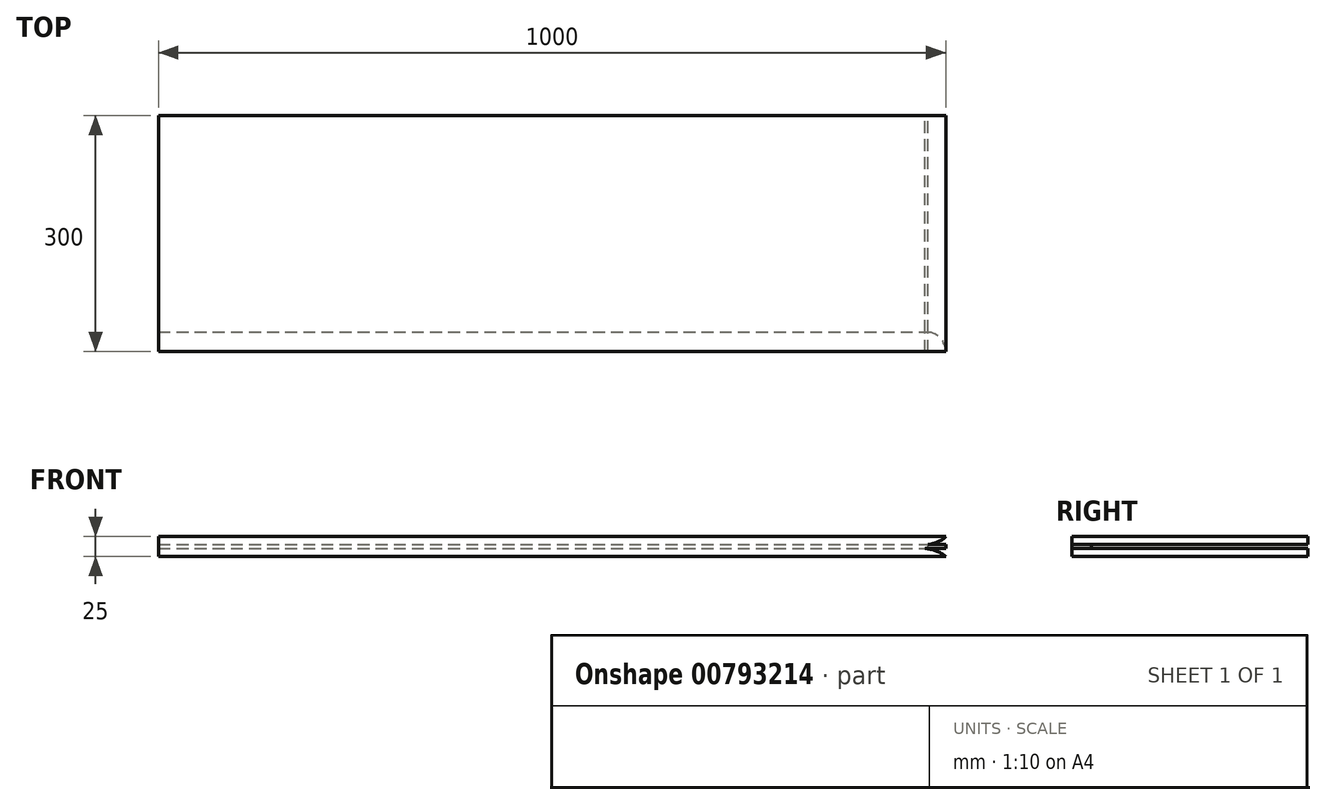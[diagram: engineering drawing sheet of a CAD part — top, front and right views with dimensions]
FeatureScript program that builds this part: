
annotation { "Feature Type Name" : "Feature", "Feature Type Description" : "" }
export const myFeature = defineFeature(function(context is Context, id is Id, definition is map)
    precondition{}
    {
        {
            var Q0;
            Q0=qCreatedBy(makeId("Top.planeOp"),FACE);
            var sketch = newSketch(context, id + "F0", { "sketchPlane" : qUnion([Q0])});
            skLineSegment(sketch, "E0.bottom", {"start": v(14.92, 154.55) * mm, "end": v(1014.92, 154.55) * mm});
            skLineSegment(sketch, "E0.top", {"start": v(14.92, -145.45) * mm, "end": v(1014.92, -145.45) * mm});
            skLineSegment(sketch, "E0.left", {"start": v(14.92, 154.55) * mm, "end": v(14.92, -145.45) * mm});
            skLineSegment(sketch, "E0.right", {"start": v(1014.92, 154.55) * mm, "end": v(1014.92, -145.45) * mm});
            skSolve(sketch);
        }
        {
            var Q0;
            Q0=makeQuery(id+"F0.imprint","IMPRINT",FACE,{"disambiguationData":[TD([[makeQuery(id+"F0.imprint","IMPRINT",EDGE,{"derivedFrom":sQuery(id+"F0.wireOp",EDGE,"E0.bottom")}),-1.0]])]});
            extrude(context, id + "F1", {"entities" : qUnion([Q0]), "depth" : 25 * mm, "offsetDistance" : 25 * mm});
        }
        {
            var Q0;
            Q0=makeQuery(id+"F1.opExtrude","SWEPT_FACE",FACE,{"disambiguationData":[OSD([sQuery(id+"F0.wireOp",EDGE,"E0.right")])]});
            var sketch = newSketch(context, id + "F2", { "sketchPlane" : qUnion([Q0])});
            skLineSegment(sketch, "E1.bottom", {"start": v(-120.45, 15) * mm, "end": v(154.55, 15) * mm});
            skLineSegment(sketch, "E1.top", {"start": v(-120.45, 10) * mm, "end": v(154.55, 10) * mm});
            skLineSegment(sketch, "E1.left", {"start": v(-120.45, 15) * mm, "end": v(-120.45, 10) * mm});
            skLineSegment(sketch, "E1.right", {"start": v(154.55, 15) * mm, "end": v(154.55, 10) * mm});
            skSolve(sketch);
        }
        {
            var Q0;
            Q0=makeQuery(id+"F2.imprint","IMPRINT",FACE,{"disambiguationData":[TD([[makeQuery(id+"F2.imprint","IMPRINT",EDGE,{"derivedFrom":sQuery(id+"F2.wireOp",EDGE,"E1.bottom")}),-1.0]])]});
            extrude(context, id + "F3", {"entities" : qUnion([Q0]), "operationType" : NewBodyOperationType.REMOVE, "endBound" : BoundingType.THROUGH_ALL, "oppositeDirection" : true, "depth" : 25 * mm, "offsetDistance" : 25 * mm});
        }
        {
            var Q0;
            {var subQ2=sQuery(id+"F0.wireOp",EDGE,"E0.bottom");Q0=makeQuery(id+"F3.boolean.opBoolean","SPLIT",FACE,{"disambiguationData":[TD([makeQuery(id+"F3.opExtrude","SWEPT_FACE",FACE,{"disambiguationData":[OSD([sQuery(id+"F2.wireOp",EDGE,"E1.bottom")])]})])],"derivedFrom":makeQuery(id+"F1.opExtrude","SWEPT_FACE",FACE,{"disambiguationData":[OSD([subQ2])]})});}
            var sketch = newSketch(context, id + "F4", { "sketchPlane" : qUnion([Q0])});
            skArc(sketch, "E2", {"start": v(-1014.92, 25) * mm, "mid": v(-1000.83, 16.83) * mm, "end": v(-984.64, 15) * mm});
            skSolve(sketch);
        }
        {
            var Q0;
            Q0 = qSketchRegion(id + "F4", true);
            var Q1;
            {var subQ0=sQuery(id+"F4.wireOp",EDGE,"E2");Q1=makeQuery(id+"F4.imprint","IMPRINT",FACE,{"disambiguationData":[TD([[makeQuery(id+"F4.imprint","IMPRINT",EDGE,{"derivedFrom":subQ0}),-1.0]])]});}
            extrude(context, id + "F5", {"entities" : qUnion([Q0, Q1]), "operationType" : NewBodyOperationType.REMOVE, "endBound" : BoundingType.THROUGH_ALL, "oppositeDirection" : true, "depth" : 25 * mm, "offsetDistance" : 25 * mm});
        }
        {
            var Q0;
            {var subQ2=sQuery(id+"F0.wireOp",EDGE,"E0.bottom");Q0=makeQuery(id+"F3.boolean.opBoolean","SPLIT",FACE,{"disambiguationData":[TD([makeQuery(id+"F3.opExtrude","SWEPT_FACE",FACE,{"disambiguationData":[OSD([sQuery(id+"F2.wireOp",EDGE,"E1.top")])]})])],"derivedFrom":makeQuery(id+"F1.opExtrude","SWEPT_FACE",FACE,{"disambiguationData":[OSD([subQ2])]})});}
            var sketch = newSketch(context, id + "F6", { "sketchPlane" : qUnion([Q0])});
            skArc(sketch, "E3", {"start": v(-979.5, 10) * mm, "mid": v(-998.13, 8.24) * mm, "end": v(-1014.92, 0) * mm});
            skSolve(sketch);
        }
        {
            var Q0;
            Q0 = qSketchRegion(id + "F6", true);
            var Q1;
            {var subQ0=sQuery(id+"F6.wireOp",EDGE,"E3");Q1=makeQuery(id+"F6.imprint","IMPRINT",FACE,{"disambiguationData":[TD([[makeQuery(id+"F6.imprint","IMPRINT",EDGE,{"derivedFrom":subQ0}),-1.0]])]});}
            extrude(context, id + "F7", {"entities" : qUnion([Q0, Q1]), "operationType" : NewBodyOperationType.REMOVE, "endBound" : BoundingType.THROUGH_ALL, "oppositeDirection" : true, "depth" : 25 * mm, "offsetDistance" : 25 * mm});
        }
        {
            var Q0;
            Q0=makeQuery(id+"F5.boolean.opBoolean","COPY",FACE,{"derivedFrom":makeQuery(id+"F5.opExtrude","SWEPT_FACE",FACE,{"disambiguationData":[OSD([sQuery(id+"F0.wireOp",EDGE,"E0.bottom"),sQuery(id+"F0.wireOp",EDGE,"E0.right"),sQuery(id+"F2.wireOp",EDGE,"E1.bottom"),sQuery(id+"F2.wireOp",EDGE,"E1.right")])]})});
            var sketch = newSketch(context, id + "F8", { "sketchPlane" : qUnion([Q0])});
            skArc(sketch, "E4", {"start": v(1014.92, -145.45) * mm, "mid": v(1008.37, -128.54) * mm, "end": v(992.13, -120.45) * mm});
            skSolve(sketch);
        }
        {
            var Q0;
            Q0=makeQuery(id+"F8.imprint","IMPRINT",FACE,{"disambiguationData":[TD([[makeQuery(id+"F8.imprint","IMPRINT",EDGE,{"derivedFrom":sQuery(id+"F8.wireOp",EDGE,"E4")}),-1.0]])]});
            extrude(context, id + "F9", {"entities" : qUnion([Q0]), "operationType" : NewBodyOperationType.REMOVE, "oppositeDirection" : true, "depth" : 5 * mm, "offsetDistance" : 25 * mm});
        }
    });
